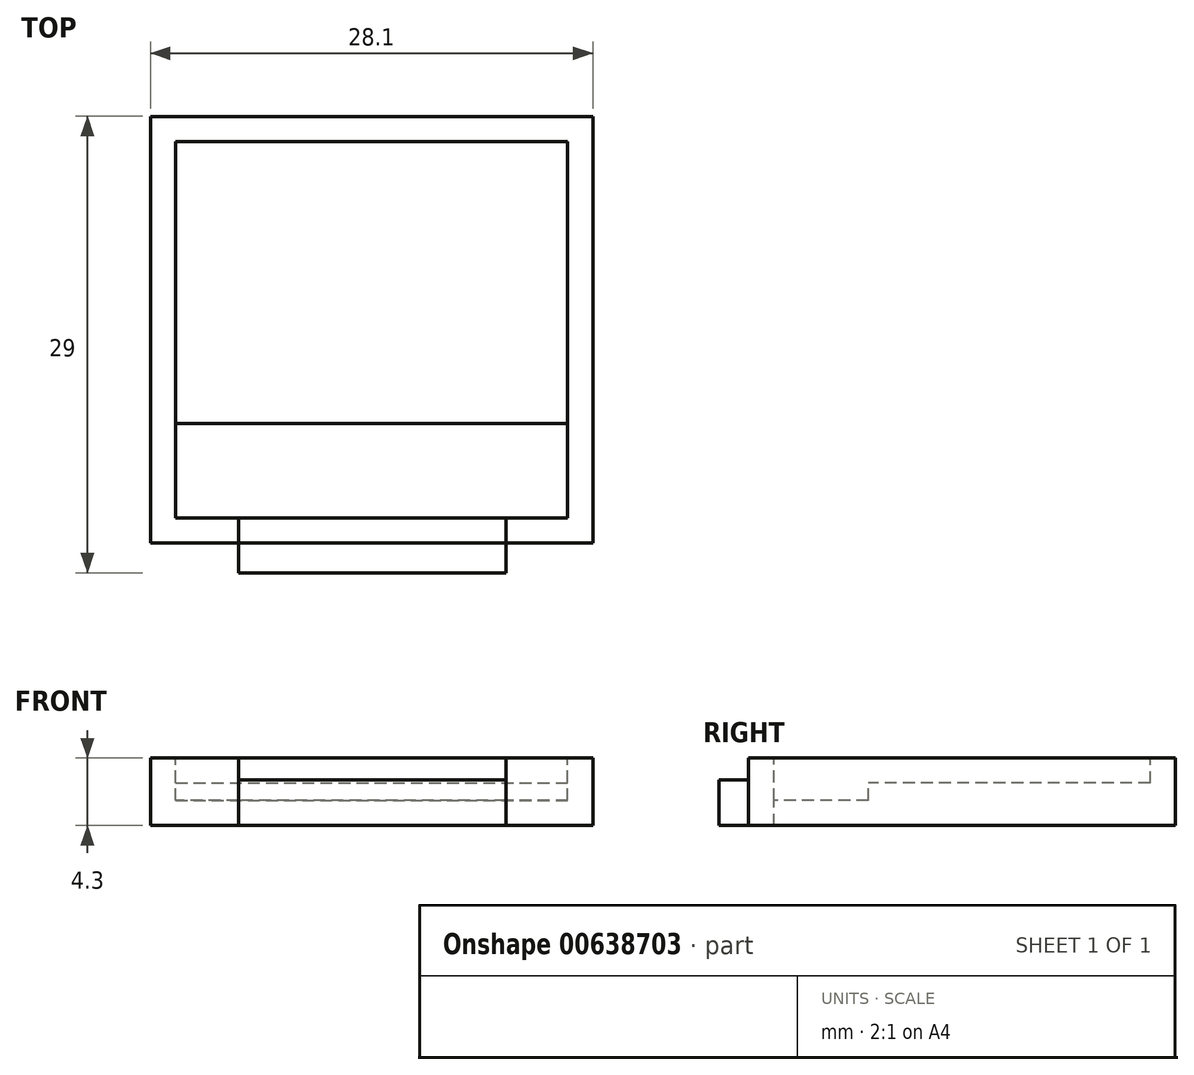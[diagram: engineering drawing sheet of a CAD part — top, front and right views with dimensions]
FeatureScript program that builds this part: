
annotation { "Feature Type Name" : "Feature", "Feature Type Description" : "" }
export const myFeature = defineFeature(function(context is Context, id is Id, definition is map)
    precondition{}
    {
        {
            var Q0;
            Q0=qCreatedBy(makeId("Top.planeOp"),FACE);
            var sketch = newSketch(context, id + "F0", { "sketchPlane" : qUnion([Q0])});
            skLineSegment(sketch, "E0.0", {"start": v(14, 14.37) * mm, "end": v(-14.1, 14.37) * mm});
            skLineSegment(sketch, "E0.1", {"start": v(14, 14.37) * mm, "end": v(14, -12.73) * mm});
            skLineSegment(sketch, "E0.2", {"start": v(14, -12.73) * mm, "end": v(-14.1, -12.73) * mm});
            skLineSegment(sketch, "E0.3", {"start": v(-14.1, 14.37) * mm, "end": v(-14.1, -12.73) * mm});
            skLineSegment(sketch, "E1.0", {"start": v(12.4, 12.77) * mm, "end": v(-12.5, 12.77) * mm});
            skLineSegment(sketch, "E1.1", {"start": v(12.4, 12.77) * mm, "end": v(12.4, -11.13) * mm});
            skLineSegment(sketch, "E1.2", {"start": v(12.4, -11.13) * mm, "end": v(-12.5, -11.13) * mm});
            skLineSegment(sketch, "E1.3", {"start": v(-12.5, 12.77) * mm, "end": v(-12.5, -11.13) * mm});
            skLineSegment(sketch, "E2", {"start": v(-12.5, -5.13) * mm, "end": v(12.4, -5.13) * mm});
            skLineSegment(sketch, "E3.bottom", {"start": v(-8.5, -11.13) * mm, "end": v(8.5, -11.13) * mm});
            skLineSegment(sketch, "E3.top", {"start": v(-8.5, -14.63) * mm, "end": v(8.5, -14.63) * mm});
            skLineSegment(sketch, "E3.left", {"start": v(-8.5, -11.13) * mm, "end": v(-8.5, -14.63) * mm});
            skLineSegment(sketch, "E3.right", {"start": v(8.5, -11.13) * mm, "end": v(8.5, -14.63) * mm});
            skPoint(sketch, "E3.middle", {"position": v(0, -12.73) * mm});
            skSolve(sketch);
        }
        {
            var Q0;
            Q0=makeQuery(id+"F0.imprint","IMPRINT",FACE,{"disambiguationData":[TD([[makeQuery(id+"F0.imprint","IMPRINT",EDGE,{"derivedFrom":sQuery(id+"F0.wireOp",EDGE,"E0.0")}),1.0]])]});
            var Q1;
            {var subQ0=sQuery(id+"F0.wireOp",EDGE,"E1.0");Q1=makeQuery(id+"F0.imprint","IMPRINT",FACE,{"disambiguationData":[TD([[makeQuery(id+"F0.imprint","IMPRINT",EDGE,{"derivedFrom":subQ0}),1.0]])]});}
            var Q2;
            {var subQ0=sQuery(id+"F0.wireOp",EDGE,"E1.2");Q2=makeQuery(id+"F0.imprint","IMPRINT",FACE,{"disambiguationData":[TD([[makeQuery(id+"F0.imprint","IMPRINT",EDGE,{"derivedFrom":subQ0}),-1.0]])]});}
            var Q3;
            {var subQ5=sQuery(id+"F0.wireOp",EDGE,"E3.bottom");Q3=makeQuery(id+"F0.imprint","IMPRINT",FACE,{"disambiguationData":[TD([[makeQuery(id+"F0.imprint","IMPRINT",EDGE,{"derivedFrom":subQ5}),-1.0]])]});}
            var Q4;
            {var subQ5=sQuery(id+"F0.wireOp",EDGE,"E3.top");Q4=makeQuery(id+"F0.imprint","IMPRINT",FACE,{"disambiguationData":[TD([[makeQuery(id+"F0.imprint","IMPRINT",EDGE,{"derivedFrom":subQ5}),1.0]])]});}
            extrude(context, id + "F1", {"entities" : qUnion([Q0, Q1, Q2, Q3, Q4]), "oppositeDirection" : true, "depth" : 4.3 * mm, "offsetDistance" : 25 * mm});
        }
        {
            var Q0;
            {var subQ0=sQuery(id+"F0.wireOp",EDGE,"E1.2");Q0=makeQuery(id+"F0.imprint","IMPRINT",FACE,{"disambiguationData":[TD([[makeQuery(id+"F0.imprint","IMPRINT",EDGE,{"derivedFrom":subQ0}),-1.0]])]});}
            extrude(context, id + "F2", {"entities" : qUnion([Q0]), "operationType" : NewBodyOperationType.REMOVE, "oppositeDirection" : true, "depth" : 2.7 * mm, "offsetDistance" : 25 * mm});
        }
        {
            var Q0;
            {var subQ0=sQuery(id+"F0.wireOp",EDGE,"E1.0");Q0=makeQuery(id+"F0.imprint","IMPRINT",FACE,{"disambiguationData":[TD([[makeQuery(id+"F0.imprint","IMPRINT",EDGE,{"derivedFrom":subQ0}),1.0]])]});}
            extrude(context, id + "F3", {"entities" : qUnion([Q0]), "operationType" : NewBodyOperationType.REMOVE, "oppositeDirection" : true, "depth" : 1.6 * mm, "offsetDistance" : 25 * mm});
        }
        {
            var Q0;
            {var subQ5=sQuery(id+"F0.wireOp",EDGE,"E3.bottom");Q0=makeQuery(id+"F0.imprint","IMPRINT",FACE,{"disambiguationData":[TD([[makeQuery(id+"F0.imprint","IMPRINT",EDGE,{"derivedFrom":subQ5}),-1.0]])]});}
            var Q1;
            {var subQ5=sQuery(id+"F0.wireOp",EDGE,"E3.top");Q1=makeQuery(id+"F0.imprint","IMPRINT",FACE,{"disambiguationData":[TD([[makeQuery(id+"F0.imprint","IMPRINT",EDGE,{"derivedFrom":subQ5}),1.0]])]});}
            extrude(context, id + "F4", {"entities" : qUnion([Q0, Q1]), "operationType" : NewBodyOperationType.REMOVE, "oppositeDirection" : true, "depth" : 1.4 * mm, "offsetDistance" : 25 * mm});
        }
    });
